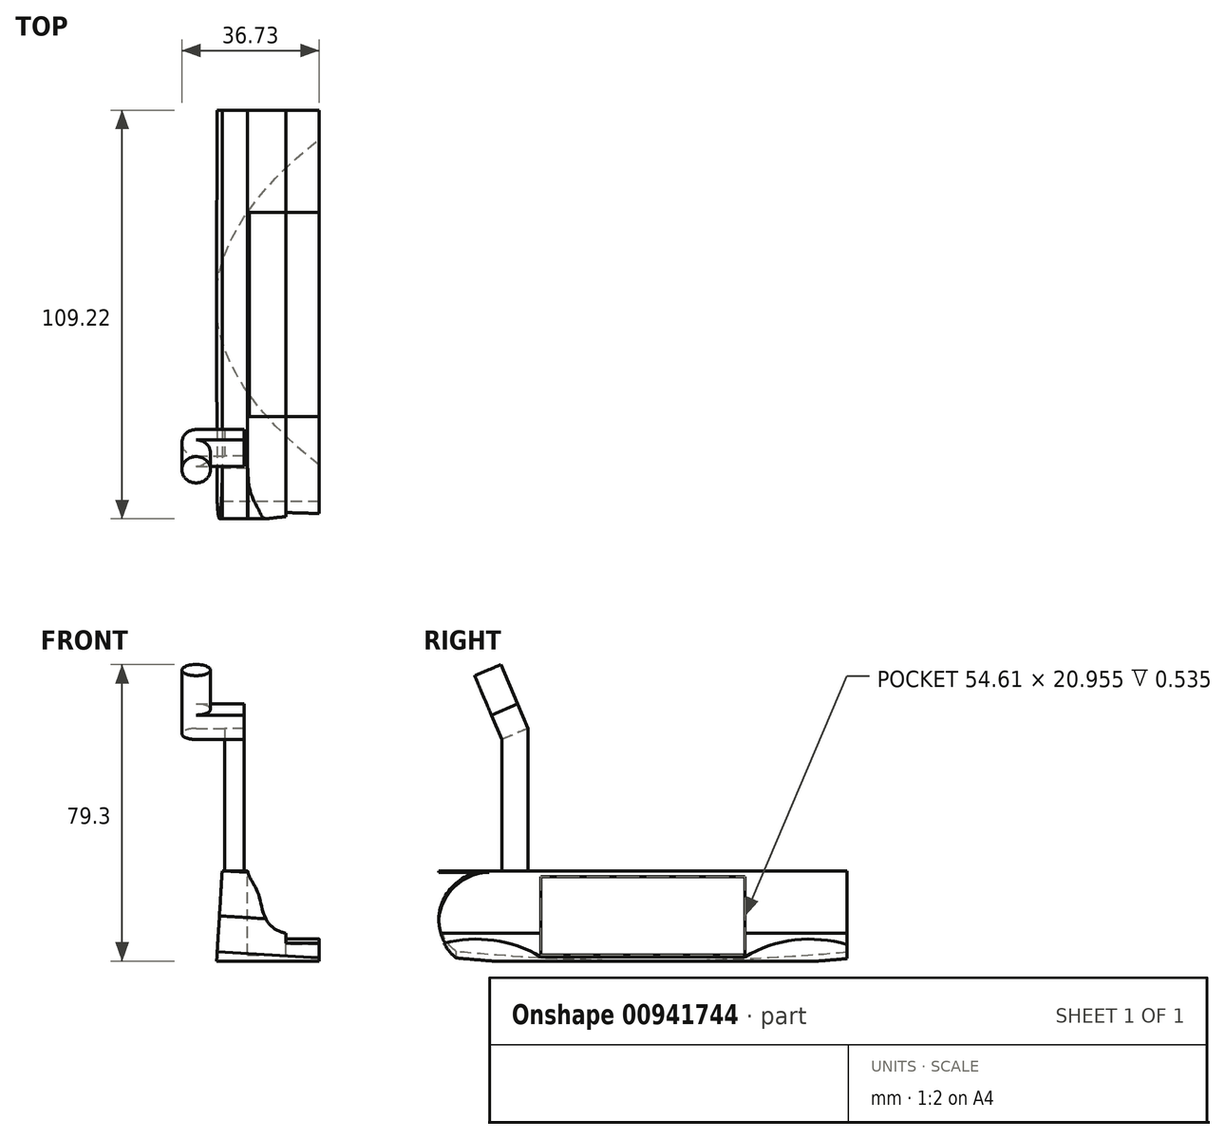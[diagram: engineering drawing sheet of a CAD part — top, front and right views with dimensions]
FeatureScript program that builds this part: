
annotation { "Feature Type Name" : "Feature", "Feature Type Description" : "" }
export const myFeature = defineFeature(function(context is Context, id is Id, definition is map)
    precondition{}
    {
        {
            var Q0;
            Q0=qCreatedBy(makeId("Right.planeOp"),FACE);
            var sketch = newSketch(context, id + "F0", { "sketchPlane" : qUnion([Q0])});
            skLineSegment(sketch, "E0.bottom", {"start": v(54.61, -12.06) * mm, "end": v(-54.61, -12.07) * mm});
            skLineSegment(sketch, "E0.top", {"start": v(54.61, 12.07) * mm, "end": v(-54.61, 12.06) * mm});
            skLineSegment(sketch, "E0.left", {"start": v(54.61, -12.06) * mm, "end": v(54.61, 12.07) * mm});
            skLineSegment(sketch, "E0.right", {"start": v(-54.61, -12.07) * mm, "end": v(-54.61, 12.06) * mm});
            skPoint(sketch, "E0.middle", {"position": v(0, 0) * mm});
            skSolve(sketch);
        }
        {
            var Q0;
            Q0=makeQuery(id+"F0.imprint","IMPRINT",FACE,{"disambiguationData":[TD([[makeQuery(id+"F0.imprint","IMPRINT",EDGE,{"derivedFrom":sQuery(id+"F0.wireOp",EDGE,"E0.bottom")}),-1.0]])]});
            extrude(context, id + "F1", {"entities" : qUnion([Q0]), "depth" : 8.25 * mm, "offsetDistance" : 25.4 * mm});
        }
        {
            var Q0;
            Q0=makeQuery(id+"F1.opExtrude","SWEPT_FACE",FACE,{"disambiguationData":[OSD([sQuery(id+"F0.wireOp",EDGE,"E0.right")])]});
            var sketch = newSketch(context, id + "F2", { "sketchPlane" : qUnion([Q0])});
            skLineSegment(sketch, "E1", {"start": v(18.54, -4.66) * mm, "end": v(18.54, -12.07) * mm});
            skLineSegment(sketch, "E2", {"start": v(18.54, -12.07) * mm, "end": v(8.26, -12.07) * mm});
            skFitSpline(sketch, "E3", {"points": [v(8.26, 12.06) * mm, v(11.22, 5.67) * mm, v(18.54, -4.66) * mm], "startDerivative": vector(1.7, -12.73) * mm, "endDerivative": vector(33.82, -7.65) * mm});
            skSolve(sketch);
        }
        {
            var Q0;
            Q0=makeQuery(id+"F2.imprint","IMPRINT",FACE,{"disambiguationData":[TD([[makeQuery(id+"F2.imprint","IMPRINT",EDGE,{"derivedFrom":sQuery(id+"F2.wireOp",EDGE,"E1")}),-1.0]])]});
            var Q1;
            Q1=makeQuery(id+"F1.opExtrude","SWEPT_FACE",FACE,{"disambiguationData":[OSD([sQuery(id+"F0.wireOp",EDGE,"E0.left")])]});
            extrude(context, id + "F3", {"entities" : qUnion([Q0]), "operationType" : NewBodyOperationType.ADD, "endBound" : BoundingType.UP_TO_SURFACE, "oppositeDirection" : true, "depth" : 25.4 * mm, "endBoundEntityFace" : qUnion([Q1]), "offsetDistance" : 25.4 * mm});
        }
        {
            var Q0;
            Q0=makeQuery(id+"F3.opExtrude","SWEPT_FACE",FACE,{"disambiguationData":[OSD([sQuery(id+"F2.wireOp",EDGE,"E1")])]});
            var sketch = newSketch(context, id + "F4", { "sketchPlane" : qUnion([Q0])});
            skLineSegment(sketch, "E4.bottom", {"start": v(27.3, -10.48) * mm, "end": v(-27.3, -10.48) * mm});
            skLineSegment(sketch, "E4.top", {"start": v(27.3, 10.48) * mm, "end": v(-27.3, 10.48) * mm});
            skLineSegment(sketch, "E4.left", {"start": v(27.3, -10.48) * mm, "end": v(27.3, 10.48) * mm});
            skLineSegment(sketch, "E4.right", {"start": v(-27.3, -10.48) * mm, "end": v(-27.3, 10.48) * mm});
            skPoint(sketch, "E4.middle", {"position": v(0, 0) * mm});
            skSolve(sketch);
        }
        {
            var Q0;
            {var subQ0=sQuery(id+"F4.wireOp",EDGE,"E4.top");Q0=makeQuery(id+"F4.imprint","IMPRINT",FACE,{"disambiguationData":[TD([[makeQuery(id+"F4.imprint","IMPRINT",EDGE,{"derivedFrom":subQ0}),1.0]])]});}
            var Q1;
            {var subQ0=sQuery(id+"F4.wireOp",EDGE,"E4.bottom");Q1=makeQuery(id+"F4.imprint","IMPRINT",FACE,{"disambiguationData":[TD([[makeQuery(id+"F4.imprint","IMPRINT",EDGE,{"derivedFrom":subQ0}),-1.0]])]});}
            extrude(context, id + "F5", {"entities" : qUnion([Q0, Q1]), "operationType" : NewBodyOperationType.REMOVE, "oppositeDirection" : true, "depth" : 10.29 * mm, "offsetDistance" : 25.4 * mm});
        }
        {
            var Q0;
            Q0=makeQuery(id+"F3.opExtrude","SWEPT_FACE",FACE,{"disambiguationData":[OSD([sQuery(id+"F2.wireOp",EDGE,"E1")])]});
            var sketch = newSketch(context, id + "F6", { "sketchPlane" : qUnion([Q0])});
            skArc(sketch, "E5", {"start": v(-27.3, -10.93) * mm, "mid": v(-40.62, -6.45) * mm, "end": v(-54.6, -7.7) * mm});
            skLineSegment(sketch, "E6", {"start": v(-27.3, -10.93) * mm, "end": v(0, -10.93) * mm});
            skPoint(sketch, "E6.endSnap0", {"position": v(0, -12.07) * mm});
            skLineSegment(sketch, "E7", {"start": v(0, -10.93) * mm, "end": v(0, -7.16) * mm});
            skLineSegment(sketch, "E8.MirrorCS", {"start": v(27.3, -10.93) * mm, "end": v(0, -10.93) * mm});
            skArc(sketch, "E9.MirrorCS", {"start": v(27.3, -10.93) * mm, "mid": v(40.62, -6.45) * mm, "end": v(54.6, -7.7) * mm});
            skLineSegment(sketch, "E10", {"start": v(-54.61, -7.7) * mm, "end": v(-54.61, -12.07) * mm});
            skLineSegment(sketch, "E11", {"start": v(-54.61, -12.07) * mm, "end": v(54.61, -12.07) * mm});
            skLineSegment(sketch, "E12", {"start": v(54.61, -12.07) * mm, "end": v(54.61, -7.7) * mm});
            skSolve(sketch);
        }
        {
            var Q0;
            Q0=makeQuery(id+"F6.imprint","IMPRINT",FACE,{"disambiguationData":[TD([[makeQuery(id+"F6.imprint","IMPRINT",EDGE,{"derivedFrom":sQuery(id+"F6.wireOp",EDGE,"E5")}),1.0]])]});
            extrude(context, id + "F7", {"entities" : qUnion([Q0]), "operationType" : NewBodyOperationType.ADD, "depth" : 8.9 * mm, "offsetDistance" : 25.4 * mm});
        }
        {
            var Q0;
            Q0=makeQuery(id+"F1.opExtrude","SWEPT_FACE",FACE,{"disambiguationData":[OSD([sQuery(id+"F0.wireOp",EDGE,"E0.top")])]});
            var sketch = newSketch(context, id + "F8", { "sketchPlane" : qUnion([Q0])});
            skLineSegment(sketch, "E13.bottom", {"start": v(7.35, -30.75) * mm, "end": v(2.14, -30.75) * mm});
            skLineSegment(sketch, "E13.top", {"start": v(7.35, -37.8) * mm, "end": v(2.14, -37.8) * mm});
            skLineSegment(sketch, "E13.left", {"start": v(7.35, -30.75) * mm, "end": v(7.35, -37.8) * mm});
            skLineSegment(sketch, "E13.right", {"start": v(2.14, -30.75) * mm, "end": v(2.14, -37.8) * mm});
            skPoint(sketch, "E13.middle", {"position": v(4.74, -34.27) * mm});
            skSolve(sketch);
        }
        {
            var Q0;
            Q0 = qSketchRegion(id + "F8", true);
            extrude(context, id + "F9", {"entities" : qUnion([Q0]), "operationType" : NewBodyOperationType.ADD, "depth" : 38.1 * mm, "offsetDistance" : 25.4 * mm});
        }
        {
            var Q0;
            Q0=makeQuery(id+"F9.opExtrude","SWEPT_FACE",FACE,{"disambiguationData":[OSD([sQuery(id+"F8.wireOp",EDGE,"E13.right")])]});
            var sketch = newSketch(context, id + "F10", { "sketchPlane" : qUnion([Q0])});
            skLineSegment(sketch, "E14", {"start": v(30.75, 50.16) * mm, "end": v(37.8, 47.18) * mm});
            skLineSegment(sketch, "E15", {"start": v(30.75, 50.16) * mm, "end": v(33.52, 56.7) * mm});
            skLineSegment(sketch, "E16", {"start": v(37.8, 47.18) * mm, "end": v(40.57, 53.73) * mm});
            skLineSegment(sketch, "E17", {"start": v(40.57, 53.73) * mm, "end": v(33.52, 56.7) * mm});
            skSolve(sketch);
        }
        {
            var Q0;
            Q0 = qSketchRegion(id + "F10", true);
            extrude(context, id + "F11", {"entities" : qUnion([Q0]), "operationType" : NewBodyOperationType.ADD, "depth" : 7.62 * mm, "offsetDistance" : 25.4 * mm});
        }
        {
            var Q0;
            Q0=makeQuery(id+"F11.opExtrude","CAP_FACE",FACE,{"disambiguationData":[OSD([sQuery(id+"F10.wireOp",EDGE,"E14"),sQuery(id+"F10.wireOp",EDGE,"E15"),sQuery(id+"F10.wireOp",EDGE,"E16"),sQuery(id+"F10.wireOp",EDGE,"E17")])],"isStart":true});
            var sketch = newSketch(context, id + "F12", { "sketchPlane" : qUnion([Q0])});
            skLineSegment(sketch, "E18", {"start": v(-33.52, 56.7) * mm, "end": v(-30.75, 50.16) * mm});
            skLineSegment(sketch, "E19", {"start": v(-30.75, 50.16) * mm, "end": v(-37.8, 47.18) * mm});
            skLineSegment(sketch, "E20", {"start": v(-37.8, 47.18) * mm, "end": v(-40.57, 53.73) * mm});
            skLineSegment(sketch, "E21", {"start": v(-40.57, 53.73) * mm, "end": v(-33.52, 56.7) * mm});
            skSolve(sketch);
        }
        {
            var Q0;
            Q0 = qSketchRegion(id + "F12", true);
            var Q1;
            Q1=makeQuery(id+"F9.opExtrude","SWEPT_FACE",FACE,{"disambiguationData":[OSD([sQuery(id+"F8.wireOp",EDGE,"E13.left")])]});
            extrude(context, id + "F13", {"entities" : qUnion([Q0]), "operationType" : NewBodyOperationType.ADD, "endBound" : BoundingType.UP_TO_SURFACE, "depth" : 25.4 * mm, "endBoundEntityFace" : qUnion([Q1]), "offsetDistance" : 25.4 * mm});
        }
        {
            var Q0;
            {var subQ0=sQuery(id+"F0.wireOp",EDGE,"E0.right");Q0=makeQuery(id+"F7.boolean.opBoolean","MERGE",FACE,{"derivedFrom":[makeQuery(id+"F3.boolean.opBoolean","MERGE",FACE,{"derivedFrom":[makeQuery(id+"F1.opExtrude","SWEPT_FACE",FACE,{"disambiguationData":[OSD([subQ0])]}),makeQuery(id+"F3.opExtrude","CAP_FACE",FACE,{"disambiguationData":[OSD([subQ0,sQuery(id+"F2.wireOp",EDGE,"0c7689a4-7c31-4f14-a8c7-f89ae6d2785b"),sQuery(id+"F2.wireOp",EDGE,"E1"),sQuery(id+"F2.wireOp",EDGE,"E2")])],"isStart":true})]}),makeQuery(id+"F7.opExtrude","SWEPT_FACE",FACE,{"disambiguationData":[OSD([sQuery(id+"F6.wireOp",EDGE,"E10")])]})]});}
            var sketch = newSketch(context, id + "F14", { "sketchPlane" : qUnion([Q0])});
            skLineSegment(sketch, "E22", {"start": v(0, -12.07) * mm, "end": v(1.48, 12.07) * mm});
            skLineSegment(sketch, "E23", {"start": v(1.48, 12.06) * mm, "end": v(8.26, 12.06) * mm});
            skLineSegment(sketch, "E24", {"start": v(8.26, 12.06) * mm, "end": v(8.26, -12.07) * mm});
            skLineSegment(sketch, "E25", {"start": v(8.26, -12.07) * mm, "end": v(0, -12.07) * mm});
            skLineSegment(sketch, "E26", {"start": v(1.48, 12.06) * mm, "end": v(0, 12.06) * mm});
            skLineSegment(sketch, "E27", {"start": v(0, 12.06) * mm, "end": v(0, -12.07) * mm});
            skSolve(sketch);
        }
        {
            var Q0;
            Q0=makeQuery(id+"F14.imprint","IMPRINT",FACE,{"disambiguationData":[TD([[makeQuery(id+"F14.imprint","IMPRINT",EDGE,{"derivedFrom":sQuery(id+"F14.wireOp",EDGE,"E22")}),1.0]])]});
            extrude(context, id + "F15", {"entities" : qUnion([Q0]), "operationType" : NewBodyOperationType.REMOVE, "endBound" : BoundingType.THROUGH_ALL, "oppositeDirection" : true, "depth" : 25.4 * mm, "offsetDistance" : 25.4 * mm});
        }
        {
            var Q0;
            Q0=makeQuery(id+"F13.boolean.opBoolean","MERGE",FACE,{"derivedFrom":[makeQuery(id+"F11.opExtrude","SWEPT_FACE",FACE,{"disambiguationData":[OSD([sQuery(id+"F10.wireOp",EDGE,"E17")])]}),makeQuery(id+"F13.opExtrude","SWEPT_FACE",FACE,{"disambiguationData":[OSD([sQuery(id+"F12.wireOp",EDGE,"E21")])]})]});
            var sketch = newSketch(context, id + "F16", { "sketchPlane" : qUnion([Q0])});
            skCircle(sketch, "E28", {"center": v(-5.48, -12.58) * mm, "radius": 3.82 * mm});
            skSolve(sketch);
        }
        {
            var Q0;
            Q0 = qSketchRegion(id + "F16", true);
            extrude(context, id + "F17", {"entities" : qUnion([Q0]), "operationType" : NewBodyOperationType.ADD, "depth" : 11.43 * mm, "offsetDistance" : 25.4 * mm});
        }
        {
            var Q0;
            Q0=makeQuery(id+"F17.opExtrude","CAP_FACE",FACE,{"disambiguationData":[OSD([sQuery(id+"F16.wireOp",EDGE,"E28")])],"isStart":true});
            var sketch = newSketch(context, id + "F18", { "sketchPlane" : qUnion([Q0])});
            skLineSegment(sketch, "E29", {"start": v(-5.48, 16.4) * mm, "end": v(-5.48, 8.75) * mm});
            skPoint(sketch, "E30.centerSnap0", {"position": v(-5.48, 12.58) * mm});
            skCircle(sketch, "E31", {"center": v(-5.48, 12.58) * mm, "radius": 3.82 * mm});
            skSolve(sketch);
        }
        {
            var Q0;
            Q0 = qSketchRegion(id + "F18", true);
            var Q1;
            Q1=makeQuery(id+"F11.opExtrude","SWEPT_FACE",FACE,{"disambiguationData":[OSD([sQuery(id+"F10.wireOp",EDGE,"E14")])]});
            extrude(context, id + "F19", {"entities" : qUnion([Q0]), "operationType" : NewBodyOperationType.ADD, "endBound" : BoundingType.UP_TO_SURFACE, "depth" : 25.4 * mm, "endBoundEntityFace" : qUnion([Q1]), "offsetDistance" : 25.4 * mm});
        }
        {
            var Q0;
            Q0 = qSketchRegion(id + "F18", true);
            var Q1;
            Q1=makeQuery(id+"F19.boolean.opBoolean","MERGE",FACE,{"derivedFrom":[makeQuery(id+"F11.opExtrude","SWEPT_FACE",FACE,{"disambiguationData":[OSD([sQuery(id+"F10.wireOp",EDGE,"E14")])]}),makeQuery(id+"F19.opExtrude","CAP_FACE",FACE,{"disambiguationData":[OSD([sQuery(id+"F18.wireOp",EDGE,"E31")])],"isStart":false})]});
            extrude(context, id + "F20", {"entities" : qUnion([Q0]), "operationType" : NewBodyOperationType.ADD, "endBound" : BoundingType.UP_TO_SURFACE, "depth" : 25.4 * mm, "endBoundEntityFace" : qUnion([Q1]), "offsetDistance" : 25.4 * mm});
        }
        {
            var Q0;
            Q0=makeQuery(id+"F15.boolean.opBoolean","COPY",FACE,{"derivedFrom":makeQuery(id+"F15.opExtrude","SWEPT_FACE",FACE,{"disambiguationData":[OSD([sQuery(id+"F14.wireOp",EDGE,"E22")])]})});
            var sketch = newSketch(context, id + "F21", { "sketchPlane" : qUnion([Q0])});
            skArc(sketch, "E32", {"start": v(40.98, -12.04) * mm, "mid": v(50.52, -9.07) * mm, "end": v(54.61, 0.05) * mm});
            skArc(sketch, "E33", {"start": v(54.61, 0.05) * mm, "mid": v(50.1, 8.7) * mm, "end": v(40.98, 12.13) * mm});
            skPoint(sketch, "E34.endSnap0", {"position": v(50.52, -9.07) * mm});
            skLineSegment(sketch, "E35", {"start": v(-54.61, -9.72) * mm, "end": v(-54.61, -12.04) * mm});
            skLineSegment(sketch, "E36", {"start": v(-54.61, -12.04) * mm, "end": v(54.61, -12.04) * mm});
            skLineSegment(sketch, "E37", {"start": v(54.61, -12.04) * mm, "end": v(54.61, -9.07) * mm});
            skLineSegment(sketch, "E38", {"start": v(0, 0) * mm, "end": v(0, -12.04) * mm});
            skArc(sketch, "E39", {"start": v(-54.61, -9.72) * mm, "mid": v(0.02, -12.04) * mm, "end": v(54.61, -9.07) * mm});
            skSolve(sketch);
        }
        {
            var Q0;
            Q0 = qSketchRegion(id + "F21", true);
            var Q1;
            {var subQ0=sQuery(id+"F21.wireOp",EDGE,"E33");var subQ1=sQuery(id+"F14.wireOp",EDGE,"E22");var subQ2=makeQuery(id+"F15.boolean.opBoolean","COPY",EDGE,{"derivedFrom":makeQuery(id+"F15.opExtrude","CAP_EDGE",EDGE,{"disambiguationData":[OSD([subQ1])],"isStart":true})});var subQ3=makeQuery(id+"F21.imprint","INTERSECT",VERTEX,{"derivedFrom":[subQ2,sQuery(id+"F21.wireOp",EDGE,"E32"),subQ0]});Q1=makeQuery(id+"F21.imprint","IMPRINT",FACE,{"disambiguationData":[TD([[makeQuery(id+"F21.imprint","IMPRINT",EDGE,{"disambiguationData":[TD([[subQ3,-1.0]])],"derivedFrom":subQ0}),-1.0]])]});}
            var Q2;
            {var subQ0=sQuery(id+"F21.wireOp",EDGE,"E32");var subQ1=makeQuery(id+"F15.boolean.opBoolean","COPY",EDGE,{"derivedFrom":makeQuery(id+"F15.opExtrude","CAP_EDGE",EDGE,{"disambiguationData":[OSD([sQuery(id+"F14.wireOp",EDGE,"E22")])],"isStart":true})});var subQ2=makeQuery(id+"F21.imprint","INTERSECT",VERTEX,{"derivedFrom":[subQ1,subQ0]});Q2=makeQuery(id+"F21.imprint","IMPRINT",FACE,{"disambiguationData":[TD([[makeQuery(id+"F21.imprint","IMPRINT",EDGE,{"disambiguationData":[TD([[subQ2,1.0]])],"derivedFrom":subQ0}),-1.0]])]});}
            extrude(context, id + "F22", {"entities" : qUnion([Q0, Q1, Q2]), "operationType" : NewBodyOperationType.REMOVE, "endBound" : BoundingType.THROUGH_ALL, "oppositeDirection" : true, "depth" : 25.4 * mm, "offsetDistance" : 25.4 * mm});
        }
    });
